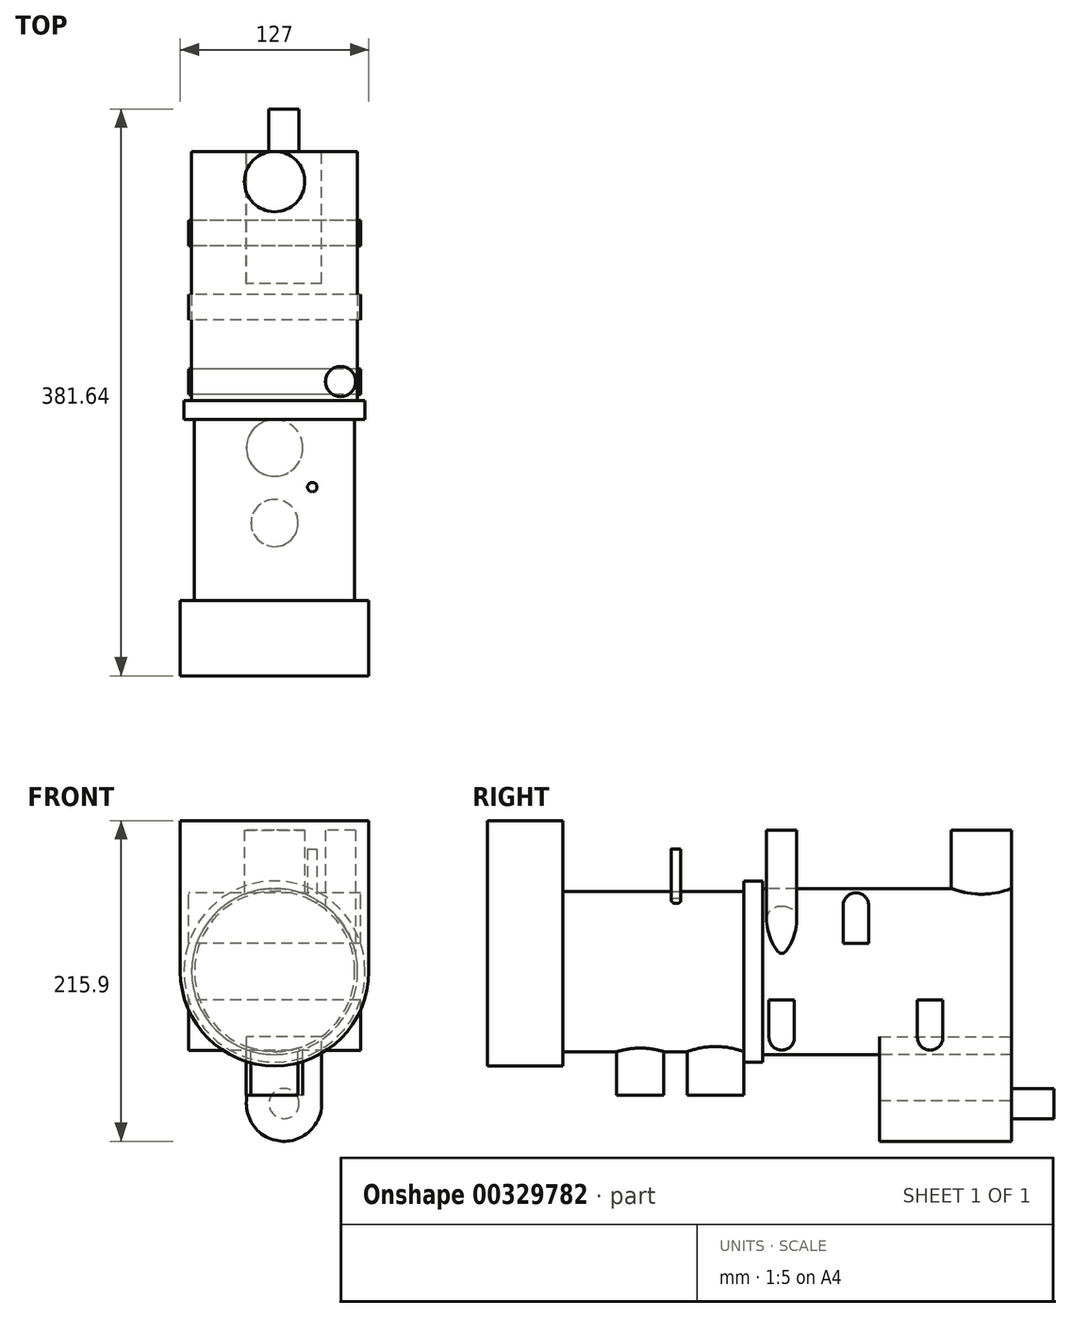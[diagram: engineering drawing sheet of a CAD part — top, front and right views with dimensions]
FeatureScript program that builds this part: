
annotation { "Feature Type Name" : "Feature", "Feature Type Description" : "" }
export const myFeature = defineFeature(function(context is Context, id is Id, definition is map)
    precondition{}
    {
        {
            var Q0;
            Q0=qCreatedBy(makeId("Front.planeOp"),FACE);
            var sketch = newSketch(context, id + "F0", { "sketchPlane" : qUnion([Q0])});
            skCircle(sketch, "E0", {"center": v(0, 0) * mm, "radius": 55.88 * mm});
            skSolve(sketch);
        }
        {
            var Q0;
            Q0 = qSketchRegion(id + "F0", true);
            extrude(context, id + "F1", {"entities" : qUnion([Q0]), "oppositeDirection" : true, "depth" : 167.64 * mm});
        }
        {
            var Q0;
            Q0=makeQuery(id+"F1.opExtrude","CAP_FACE",FACE,{"disambiguationData":[OSD([sQuery(id+"F0.wireOp",EDGE,"E0")])],"isStart":true});
            var sketch = newSketch(context, id + "F2", { "sketchPlane" : qUnion([Q0])});
            skCircle(sketch, "E1", {"center": v(0, 0) * mm, "radius": 60.96 * mm});
            skSolve(sketch);
        }
        {
            var Q0;
            Q0 = qSketchRegion(id + "F2", true);
            extrude(context, id + "F3", {"entities" : qUnion([Q0]), "operationType" : NewBodyOperationType.ADD, "depth" : 12.7 * mm});
        }
        {
            var Q0;
            Q0=makeQuery(id+"F3.opExtrude","CAP_FACE",FACE,{"disambiguationData":[OSD([sQuery(id+"F2.wireOp",EDGE,"E1")])],"isStart":false});
            var sketch = newSketch(context, id + "F4", { "sketchPlane" : qUnion([Q0])});
            skCircle(sketch, "E2", {"center": v(0, 0) * mm, "radius": 53.98 * mm});
            skSolve(sketch);
        }
        {
            var Q0;
            Q0 = qSketchRegion(id + "F4", true);
            extrude(context, id + "F5", {"entities" : qUnion([Q0]), "operationType" : NewBodyOperationType.ADD, "depth" : 121.92 * mm});
        }
        {
            var Q0;
            Q0=makeQuery(id+"F5.opExtrude","CAP_FACE",FACE,{"disambiguationData":[OSD([sQuery(id+"F4.wireOp",EDGE,"E2")])],"isStart":false});
            var sketch = newSketch(context, id + "F6", { "sketchPlane" : qUnion([Q0])});
            skArc(sketch, "E3", {"start": v(-63.5, 0) * mm, "mid": v(0, -63.5) * mm, "end": v(63.5, 0) * mm});
            skLineSegment(sketch, "E4.top", {"start": v(63.5, 101.6) * mm, "end": v(-63.5, 101.6) * mm});
            skLineSegment(sketch, "E4.left", {"start": v(63.5, 0) * mm, "end": v(63.5, 101.6) * mm});
            skLineSegment(sketch, "E4.right", {"start": v(-63.5, 0) * mm, "end": v(-63.5, 101.6) * mm});
            skSolve(sketch);
        }
        {
            var Q0;
            Q0 = qSketchRegion(id + "F6", true);
            extrude(context, id + "F7", {"entities" : qUnion([Q0]), "operationType" : NewBodyOperationType.ADD, "depth" : 50.8 * mm});
        }
        {
            var Q0;
            Q0=qCreatedBy(makeId("Right.planeOp"),FACE);
            var sketch = newSketch(context, id + "F8", { "sketchPlane" : qUnion([Q0])});
            skArc(sketch, "E5", {"start": v(4.13, -44.45) * mm, "mid": v(12.7, -53.02) * mm, "end": v(21.27, -44.45) * mm});
            skArc(sketch, "E6", {"start": v(104.13, -44.45) * mm, "mid": v(112.7, -53.02) * mm, "end": v(121.27, -44.45) * mm});
            skArc(sketch, "E7", {"start": v(71.27, 44.45) * mm, "mid": v(62.7, 53.02) * mm, "end": v(54.13, 44.45) * mm});
            skLineSegment(sketch, "E8.top", {"start": v(4.13, -19.05) * mm, "end": v(21.27, -19.05) * mm});
            skLineSegment(sketch, "E8.left", {"start": v(4.13, -44.45) * mm, "end": v(4.13, -19.05) * mm});
            skLineSegment(sketch, "E8.right", {"start": v(21.27, -44.45) * mm, "end": v(21.27, -19.05) * mm});
            skLineSegment(sketch, "E9.top", {"start": v(104.13, -19.05) * mm, "end": v(121.27, -19.05) * mm});
            skLineSegment(sketch, "E9.left", {"start": v(104.13, -44.45) * mm, "end": v(104.13, -19.05) * mm});
            skLineSegment(sketch, "E9.right", {"start": v(121.27, -44.45) * mm, "end": v(121.27, -19.05) * mm});
            skLineSegment(sketch, "E10.bottom", {"start": v(54.13, 19.06) * mm, "end": v(71.27, 19.06) * mm});
            skLineSegment(sketch, "E10.left", {"start": v(54.13, 19.06) * mm, "end": v(54.13, 44.45) * mm});
            skLineSegment(sketch, "E10.right", {"start": v(71.27, 19.06) * mm, "end": v(71.27, 44.46) * mm});
            skSolve(sketch);
        }
        {
            var Q0;
            Q0 = qSketchRegion(id + "F8", true);
            extrude(context, id + "F9", {"entities" : qUnion([Q0]), "depth" : 58 * mm, "hasSecondDirection" : true, "secondDirectionOppositeDirection" : true, "secondDirectionDepth" : 58 * mm});
        }
        {
            var Q0;
            Q0=qCreatedBy(makeId("Top.planeOp"),FACE);
            var sketch = newSketch(context, id + "F10", { "sketchPlane" : qUnion([Q0])});
            skCircle(sketch, "E11", {"center": v(0, -32) * mm, "radius": 19.05 * mm});
            skCircle(sketch, "E12", {"center": v(0, -82.55) * mm, "radius": 15.88 * mm});
            skSolve(sketch);
        }
        {
            var Q0;
            Q0 = qSketchRegion(id + "F10", true);
            extrude(context, id + "F11", {"entities" : qUnion([Q0]), "operationType" : NewBodyOperationType.ADD, "oppositeDirection" : true, "depth" : 83.18 * mm});
        }
        {
            var Q0;
            Q0=makeQuery(id+"F1.opExtrude","CAP_FACE",FACE,{"disambiguationData":[OSD([sQuery(id+"F0.wireOp",EDGE,"E0")])],"isStart":false});
            var sketch = newSketch(context, id + "F12", { "sketchPlane" : qUnion([Q0])});
            skArc(sketch, "E13", {"start": v(-31.75, -88.82) * mm, "mid": v(-5.38, -114.28) * mm, "end": v(18.97, -86.88) * mm});
            skLineSegment(sketch, "E14.top", {"start": v(-31.75, -43.81) * mm, "end": v(18.97, -43.81) * mm});
            skLineSegment(sketch, "E14.left", {"start": v(-31.75, -88.98) * mm, "end": v(-31.75, -43.81) * mm});
            skLineSegment(sketch, "E14.right", {"start": v(18.97, -88.98) * mm, "end": v(18.97, -43.81) * mm});
            skSolve(sketch);
        }
        {
            var Q0;
            Q0 = qSketchRegion(id + "F12", true);
            extrude(context, id + "F13", {"entities" : qUnion([Q0]), "oppositeDirection" : true, "depth" : 88.9 * mm});
        }
        {
            var Q0;
            Q0=makeQuery(id+"F13.opExtrude","CAP_FACE",FACE,{"disambiguationData":[OSD([sQuery(id+"F12.wireOp",EDGE,"E13"),sQuery(id+"F12.wireOp",EDGE,"E14.top"),sQuery(id+"F12.wireOp",EDGE,"E14.left"),sQuery(id+"F12.wireOp",EDGE,"E14.right")])],"isStart":true});
            var sketch = newSketch(context, id + "F14", { "sketchPlane" : qUnion([Q0])});
            skCircle(sketch, "E15", {"center": v(-6.35, -88.9) * mm, "radius": 10.16 * mm});
            skSolve(sketch);
        }
        {
            var Q0;
            Q0 = qSketchRegion(id + "F14", true);
            extrude(context, id + "F15", {"entities" : qUnion([Q0]), "operationType" : NewBodyOperationType.ADD, "depth" : 28.57 * mm});
        }
        {
            var Q0;
            Q0=qCreatedBy(makeId("Top.planeOp"),FACE);
            var sketch = newSketch(context, id + "F16", { "sketchPlane" : qUnion([Q0])});
            skCircle(sketch, "E16", {"center": v(0, 147.32) * mm, "radius": 20.32 * mm});
            skCircle(sketch, "E17", {"center": v(44.45, 12.7) * mm, "radius": 10.16 * mm});
            skSolve(sketch);
        }
        {
            var Q0;
            Q0 = qSketchRegion(id + "F16", true);
            extrude(context, id + "F17", {"entities" : qUnion([Q0]), "operationType" : NewBodyOperationType.ADD, "depth" : 95.25 * mm});
        }
        {
            var Q0;
            Q0=qCreatedBy(makeId("Top.planeOp"),FACE);
            var sketch = newSketch(context, id + "F18", { "sketchPlane" : qUnion([Q0])});
            skCircle(sketch, "E18", {"center": v(25.4, -58.42) * mm, "radius": 3.18 * mm});
            skSolve(sketch);
        }
        {
            var Q0;
            Q0 = qSketchRegion(id + "F18", true);
            extrude(context, id + "F19", {"entities" : qUnion([Q0]), "operationType" : NewBodyOperationType.ADD, "depth" : 82.55 * mm});
        }
    });
